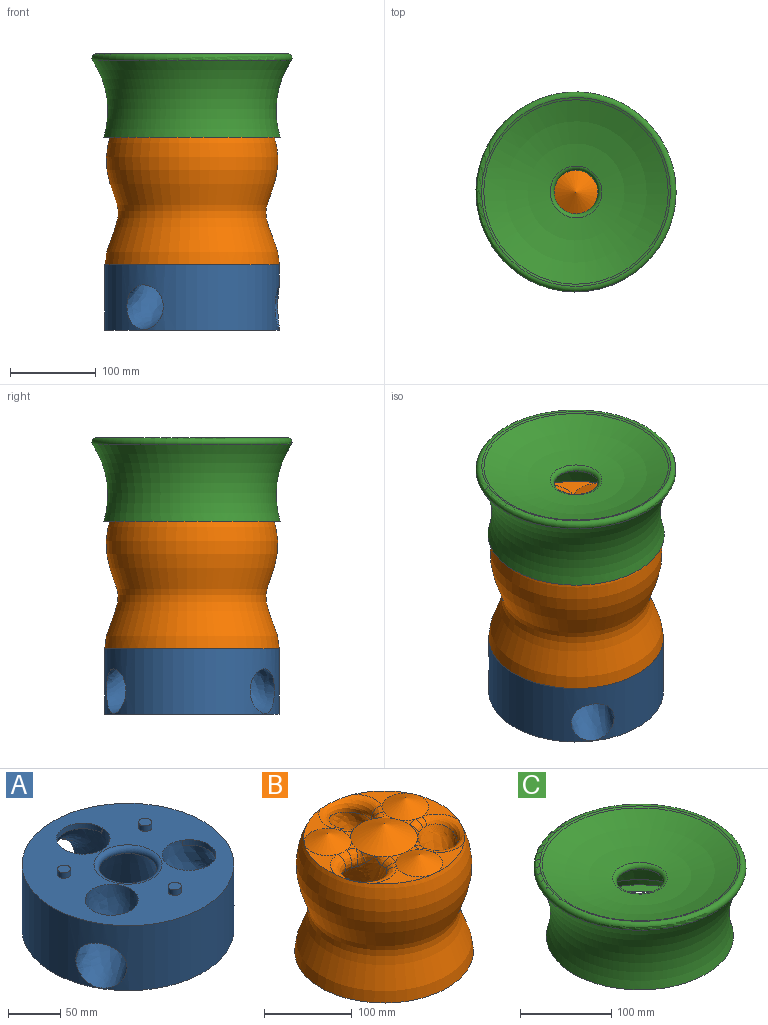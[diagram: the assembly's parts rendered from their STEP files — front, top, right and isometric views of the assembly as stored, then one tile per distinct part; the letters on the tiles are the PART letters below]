
ASSEMBLY  parts=3 mates=3
PART A: 20 faces, bbox 223.2x223.7x86.9 mm
  f0: cylinder r=101.6mm len=203.2mm, axis (0,0,-1), area 42377.7mm2, adj f1,f2,f7,f8,f9
  f1: plane 207.6x207.6mm, normal (0,0,1), area 22512.6mm2, adj f0,f3,f4,f5,f6,f7,f8,f9
  f2: plane 203.2x203.2mm, normal (0,0,-1), area 32429.3mm2, adj f0
  f3: cylinder r=25.4mm len=47.63mm, axis (0,0,1), area 509.7mm2, adj f1,f8
  f4: cylinder r=25.4mm len=47.63mm, axis (0,0,1), area 509.7mm2, adj f1,f9
  f5: cylinder r=25.4mm len=50.8mm, axis (0,0,1), area 509.7mm2, adj f1,f6,f7
  f6: bspline ~6.4x1.41mm, area 1.5mm2, adj f1,f5,f7
  f7: bspline ~82.72x78.09mm, area 10157.9mm2, adj f0,f1,f5,f6
  f8: bspline ~82.79x77.92mm, area 10164.4mm2, adj f0,f1,f3
  f9: bspline ~82.39x78.31mm, area 10158.7mm2, adj f0,f1,f4
  f10: cone r=25.4mm half-angle=20deg, axis (0,0,-1), area 14325.3mm2, adj f18,f19
  f11: plane 87.14x87.14mm, normal (0,0,1), area 5963.4mm2, adj f19
  f12: cylinder r=6.35mm len=12.7mm, axis (0,0,-1), area 253.4mm2, adj f1,f13
  f13: plane 12.7x12.7mm, normal (0,0,1), area 126.7mm2, adj f12
  f14: cylinder r=6.35mm len=12.7mm, axis (0,0,-1), area 253.4mm2, adj f1,f15
  f15: plane 12.7x12.7mm, normal (0,0,1), area 126.7mm2, adj f14
  f16: cylinder r=6.35mm len=12.7mm, axis (0,0,-1), area 253.4mm2, adj f1,f17
  f17: plane 12.7x12.7mm, normal (0,0,1), area 126.7mm2, adj f16
  f18: torus R=32.65mm, axis (0,0,1), area 1783.5mm2, adj f1,f10
  f19: torus R=43.57mm, axis (0,0,1), area 2887.4mm2, adj f10,f11
PART B: 51 faces, bbox 203.2x203.2x177.8 mm
  f0: bspline ~13.97x12.76mm, area 66.9mm2, adj f14,f18,f38
  f1: bspline ~17.66x11.4mm, area 66.9mm2, adj f14,f19,f31
  f2: bspline ~17.84x11.4mm, area 32.3mm2, adj f14,f20,f24
  f3: plane 17.16x16.35mm, normal (0,0,1), area 64.6mm2, adj f14,f21,f43
  f4: plane 70.12x31.51mm, normal (0,0,1), area 627.6mm2, adj f16,f21,f41
  f5: plane 66.13x31.23mm, normal (0,0,1), area 583.2mm2, adj f16,f23,f41
  f6: plane 21.11x12.69mm, normal (0,0,1), area 64.6mm2, adj f14,f23,f36
  f7: plane 61.04x39.52mm, normal (0,0,1), area 627.6mm2, adj f16,f23,f34
  f8: plane 66.16x30.03mm, normal (0,0,1), area 583.2mm2, adj f16,f22,f34
  f9: plane 21.62x13.37mm, normal (0,0,1), area 64.6mm2, adj f14,f22,f29
  f10: plane 60.41x38.01mm, normal (0,0,1), area 627.6mm2, adj f16,f22,f27
  f11: plane 48.46x48.39mm, normal (0,0,1), area 583.2mm2, adj f16,f21,f27
  f12: plane 16.85x15.21mm, normal (0,0,1), area 54.3mm2, adj f14,f22,f32
  f13: plane 17.31x11.12mm, normal (0,0,1), area 54.3mm2, adj f14,f23,f39
  f14: cone r=0mm half-angle=63.4deg, axis (0,0,-1), area 5098.6mm2, adj f0,f1,f2,f3,f6,f9,f12,f13
  f15: plane 203.2x203.2mm, normal (0,0,-1), area 27046.3mm2, adj f16,f18,f19,f20,f45,f47,f49
  f16: revolved ~203.2x203.2mm, area 97734.8mm2, adj f4,f5,f7,f8,f10,f11,f15,f27
  f17: plane 19.72x9.74mm, normal (0,0,1), area 54.3mm2, adj f14,f21,f25
  f18: bspline ~158.75x131.94mm, area 23051.7mm2, adj f0,f15,f38,f39,f40,f41,f42,f43
  f19: bspline ~158.75x130.61mm, area 23052mm2, adj f1,f15,f31,f32,f33,f34,f35,f36
  f20: bspline ~158.75x110.48mm, area 23053.2mm2, adj f2,f15,f24,f25,f26,f27,f28,f29
  f21: cone r=26.67mm half-angle=65deg, axis (0,0,-1), area 2465.6mm2, adj f3,f4,f11,f17,f26,f42
  f22: cone r=26.67mm half-angle=65deg, axis (0,0,-1), area 2465.6mm2, adj f8,f9,f10,f12,f28,f33
  f23: cone r=26.67mm half-angle=65deg, axis (0,0,-1), area 2465.6mm2, adj f5,f6,f7,f13,f35,f40
  f24: bspline ~17.01x16.39mm, area 131mm2, adj f2,f14,f20,f25
  f25: bspline ~23.9x20.28mm, area 212.3mm2, adj f17,f20,f24,f26
  f26: bspline ~22.83x21.74mm, area 263.2mm2, adj f20,f21,f25,f27
  f27: bspline ~75.63x49.88mm, area 1961.5mm2, adj f10,f11,f16,f20,f26,f28
  f28: bspline ~14.05x12.55mm, area 92mm2, adj f20,f22,f27,f29
  f29: bspline ~20.29x20.15mm, area 163.2mm2, adj f9,f20,f28,f30
  f30: bspline ~17.76x10.3mm, area 0mm2, adj f14,f20,f29
  f31: bspline ~17.22x17.01mm, area 131mm2, adj f1,f14,f19,f32
  f32: bspline ~21x20.58mm, area 212.3mm2, adj f12,f19,f31,f33
  f33: bspline ~23.04x20.11mm, area 263.2mm2, adj f19,f22,f32,f34
  f34: bspline ~74.87x61.11mm, area 2123.6mm2, adj f7,f8,f16,f19,f33,f35
  f35: bspline ~16.8x16.05mm, area 92mm2, adj f19,f23,f34,f36
  f36: bspline ~19.53x15.55mm, area 163.2mm2, adj f6,f19,f35,f37
  f37: bspline ~13.18x12.68mm, area 96.7mm2, adj f14,f19,f36
  f38: bspline ~18.01x17.01mm, area 131mm2, adj f0,f14,f18,f39
  f39: bspline ~21.52x18.66mm, area 212.3mm2, adj f13,f18,f38,f40
  f40: bspline ~24.94x20.11mm, area 263.2mm2, adj f18,f23,f39,f41
  f41: bspline ~72.78x66.24mm, area 2123.5mm2, adj f4,f5,f16,f18,f40,f42
  f42: bspline ~12.35x10.56mm, area 92mm2, adj f18,f21,f41,f43
  f43: bspline ~20.17x15.11mm, area 163.2mm2, adj f3,f18,f42,f44
  f44: bspline ~17.58x10.39mm, area 52.8mm2, adj f14,f18,f43
  f45: cylinder r=6.99mm len=13.97mm, axis (0,0,-1), area 334.4mm2, adj f15,f46
  f46: plane 13.97x13.97mm, normal (0,0,-1), area 153.3mm2, adj f45
  f47: cylinder r=6.99mm len=13.97mm, axis (0,0,-1), area 334.4mm2, adj f15,f48
  f48: plane 13.97x13.97mm, normal (0,0,-1), area 153.3mm2, adj f47
  f49: cylinder r=6.99mm len=13.97mm, axis (0,0,-1), area 334.4mm2, adj f15,f50
  f50: plane 13.97x13.97mm, normal (0,0,-1), area 153.3mm2, adj f49
PART C: 12 faces, bbox 278.3x278.3x149.8 mm
  f0: revolved ~192.76x192.76mm, area 13556.7mm2, adj f3,f10
  f1: torus R=12.81mm, axis (0,0,1), area 34701.8mm2, adj f6,f8
  f2: cone r=12.59mm half-angle=66.6deg, axis (0,0,-1), area 14816.9mm2, adj f3,f9
  f3: torus R=10.76mm, axis (0,0,1), area 24208.7mm2, adj f0,f2
  f4: plane 205.31x205.31mm, normal (0,0,-1), area 11147.2mm2, adj f5,f11
  f5: torus R=203.45mm, axis (0,0,1), area 60046.1mm2, adj f4,f7
  f6: torus R=117.26mm, axis (0,0,-1), area 1843.9mm2, adj f1,f7
  f7: torus R=111.33mm, axis (0,0,-1), area 8959.8mm2, adj f5,f6
  f8: torus R=30.48mm, axis (0,0,1), area 1296.6mm2, adj f1,f9
  f9: torus R=29.5mm, axis (0,0,1), area 446mm2, adj f2,f8
  f10: plane 192.76x192.76mm, normal (0,0,1), area 7223.4mm2, adj f0,f11
  f11: cylinder r=83.61mm len=167.21mm, axis (0,0,-1), area 262.7mm2, adj f4,f10
PLACE A rot(axis=(0,0,1),26.3deg) t=(-21.34,-35.93,-200.5)mm
PLACE B t=(-21.34,-35.93,53.5)mm fixed
PLACE C rot(axis=(0,0,1),61.1deg) t=(0.79,4.23,-28.65)mm
MATE planar B.f14 <-> A.f10  axis (0,0,-1) through (-21.34,-35.93,-124.3)mm
MATE cylindrical A.f0 <-> B.f14  axis (0,0,1) through (-21.34,-35.93,-124.3)mm
MATE cylindrical A.f0 <-> C.f1  axis (0,0,-1) through (-21.34,-35.93,-162.4)mm
